# Revit family: NX_Low_Mount_Indoor_Sensor_Module
name_source: partatom
category: Communication Devices
revit_build: Autodesk Revit 2014 (Build: 20130308_1515(x64)
units: mm (PartAtom-declared; Revit-internal decimal feet)

## types (1)
- NX_Low_Mount_Indoor_Sensor_Module
    Assembly Code = D5090
    Black = Paint - Hubbell - Carbon Black
    Certifications = Bluetooth® Version 4.1,FCC Part 15.247,FCC ID: YH9NXSMP,IC: 9044A-NXSMP
    Coverage = 1:1 (mounting height : coverage radius) up to 14’, min 8’
    Default Elevation = 48 "
    Description = The Hubbell Control Solutions NXSMP Low Mount Sensor Indoor Module provides a unique solution for integrating automatic control functions directly into a luminaire.
    Features = •Compact, discrete, low profile luminaire sensor •
PIR motion sensor for automatic On/Off control
•Integrated daylight sensor for daylight harvesting and/or lumen maintenance
•
Bluetooth radio provides wireless control of luminaire
•
Easy sensor configuration using smart device App
•Enables Intelliscope™ feature when paired with NX Bluetooth mobile App, providing real time visibility of motion for improved accuracy of sensor sensitivity and time delay adjustments
•Non-volatile memory for sensor settings
•
Simple plug-in connection to NX Fixture Modules
    Manufacturer = Hubbell Control Solutions
    Model = Low Mount Indoor Sensor Module
    Mounting = Mounts in 1.2” diameter aperture, secured by supplied nut on threaded body
Recommended max mounting height: 14 ft. [4.27 m], min 8’
    Product Documentation Link = https://hubbellcdn.com
    Product Page URL = https://www.hubbell.com
    Sensor Type = Low Mount Indoor
    Standby Power = 120VAC: 0.1,277VAC: 0.1,347VAC: 0.2
    Technology = Passive Infrared
    Timer Timeout = Automatic mode: 1 sec – 20 min
    Type Comments = Low Mount Indoor Sensor Module
    URL = https://www.hubbell.com
    Warranty = 5-Years Warranty
    White = Paint - Hubbell - Matte White
    Width = 1.6 "

## geometry (parser evidence)
native form markers: Sweep x1
no freeform markers — native parametric forms only
